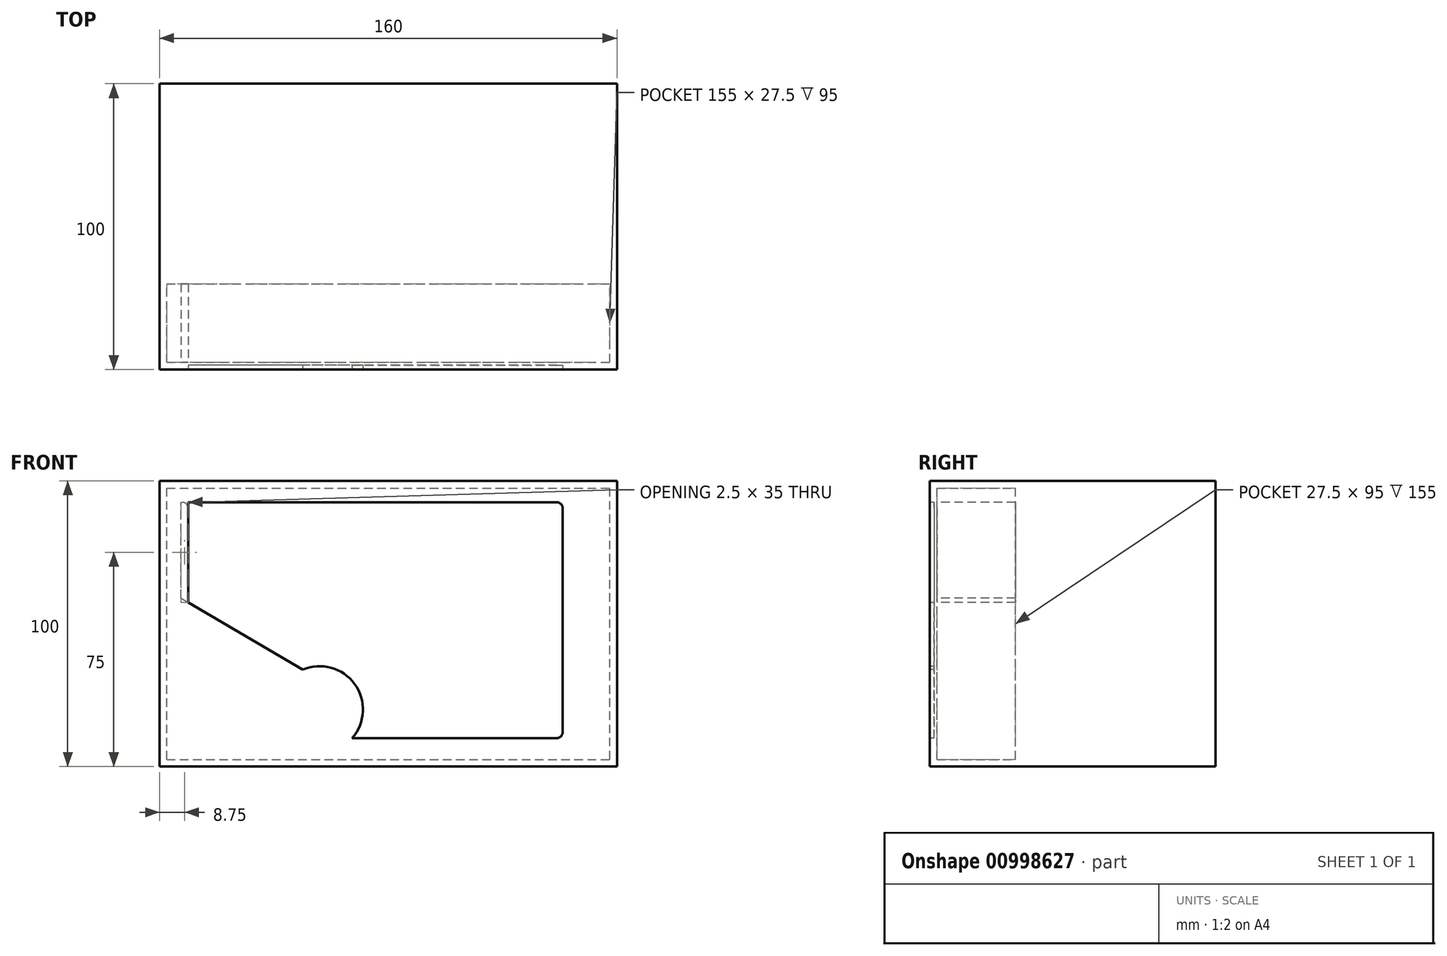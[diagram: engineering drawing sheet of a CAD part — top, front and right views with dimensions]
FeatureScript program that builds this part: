
annotation { "Feature Type Name" : "Feature", "Feature Type Description" : "" }
export const myFeature = defineFeature(function(context is Context, id is Id, definition is map)
    precondition{}
    {
        {
            var Q0;
            Q0=qCreatedBy(makeId("Front.planeOp"),FACE);
            var sketch = newSketch(context, id + "F0", { "sketchPlane" : qUnion([Q0])});
            skLineSegment(sketch, "E0.bottom", {"start": v(0, 0) * mm, "end": v(160, 0) * mm});
            skLineSegment(sketch, "E0.top", {"start": v(0, 100) * mm, "end": v(160, 100) * mm});
            skLineSegment(sketch, "E0.left", {"start": v(0, 0) * mm, "end": v(0, 100) * mm});
            skLineSegment(sketch, "E0.right", {"start": v(160, 0) * mm, "end": v(160, 100) * mm});
            skSolve(sketch);
        }
        {
            var Q0;
            Q0 = qSketchRegion(id + "F0", true);
            extrude(context, id + "F1", {"entities" : qUnion([Q0]), "depth" : 100 * mm, "offsetDistance" : 25 * mm});
        }
        {
            var Q0;
            Q0=makeQuery(id+"F1.opExtrude","CAP_FACE",FACE,{"disambiguationData":[OSD([sQuery(id+"F0.wireOp",EDGE,"E0.bottom"),sQuery(id+"F0.wireOp",EDGE,"E0.top"),sQuery(id+"F0.wireOp",EDGE,"E0.left"),sQuery(id+"F0.wireOp",EDGE,"E0.right")])],"isStart":false});
            var sketch = newSketch(context, id + "F2", { "sketchPlane" : qUnion([Q0])});
            skLineSegment(sketch, "E1.bottom", {"start": v(0, 0) * mm, "end": v(160, 0) * mm});
            skLineSegment(sketch, "E1.top", {"start": v(0, 100) * mm, "end": v(160, 100) * mm});
            skLineSegment(sketch, "E1.right", {"start": v(160, 0) * mm, "end": v(160, 100) * mm});
            skLineSegment(sketch, "E2", {"start": v(141, 50) * mm, "end": v(141, 92.5) * mm});
            skLineSegment(sketch, "E3", {"start": v(80, 10) * mm, "end": v(67.37, 10) * mm});
            skLineSegment(sketch, "E4.top", {"start": v(10, 92.5) * mm, "end": v(141, 92.5) * mm});
            skLineSegment(sketch, "E4.left", {"start": v(10, 57.5) * mm, "end": v(10, 92.5) * mm});
            skLineSegment(sketch, "E4.right", {"start": v(141, 10) * mm, "end": v(141, 92.5) * mm});
            skLineSegment(sketch, "E5", {"start": v(10, 92.5) * mm, "end": v(10, 57.5) * mm});
            skLineSegment(sketch, "E6", {"start": v(10, 57.5) * mm, "end": v(50, 33.9) * mm});
            skLineSegment(sketch, "E7", {"start": v(0, 0) * mm, "end": v(56, 0) * mm});
            skArc(sketch, "E8", {"start": v(67.37, 10) * mm, "mid": v(68.25, 28.9) * mm, "end": v(50, 33.9) * mm});
            skLineSegment(sketch, "E9.trimOffspring", {"start": v(67.37, 10) * mm, "end": v(141, 10) * mm});
            skPoint(sketch, "E10.start.orphan", {"position": v(80, 0) * mm});
            skPoint(sketch, "E11.start.orphan", {"position": v(160, 50) * mm});
            skPoint(sketch, "E12.end.orphan", {"position": v(80, 92.5) * mm});
            skPoint(sketch, "E12.start.orphan", {"position": v(80, 100) * mm});
            skSolve(sketch);
        }
        {
            var Q0;
            {var subQ1=sQuery(id+"F2.wireOp",EDGE,"E4.top");Q0=makeQuery(id+"F2.imprint","IMPRINT",FACE,{"disambiguationData":[TD([[makeQuery(id+"F2.imprint","IMPRINT",EDGE,{"derivedFrom":subQ1}),-1.0]])]});}
            extrude(context, id + "F3", {"entities" : qUnion([Q0]), "operationType" : NewBodyOperationType.REMOVE, "oppositeDirection" : true, "depth" : 50 * mm, "offsetDistance" : 25 * mm});
        }
        {
            var Q0;
            Q0=makeQuery(id+"F3.boolean.opBoolean","COPY",FACE,{"derivedFrom":makeQuery(id+"F3.opExtrude","SWEPT_FACE",FACE,{"disambiguationData":[OSD([sQuery(id+"F2.wireOp",EDGE,"E5")])]})});
            var Q1;
            Q1=makeQuery(id+"F3.boolean.opBoolean","COPY",FACE,{"derivedFrom":makeQuery(id+"F3.opExtrude","SWEPT_FACE",FACE,{"disambiguationData":[OSD([sQuery(id+"F2.wireOp",EDGE,"E6")])]})});
            var Q2;
            Q2=makeQuery(id+"F3.boolean.opBoolean","COPY",FACE,{"derivedFrom":makeQuery(id+"F3.opExtrude","SWEPT_FACE",FACE,{"disambiguationData":[OSD([sQuery(id+"F2.wireOp",EDGE,"E8")])]})});
            var Q3;
            Q3=makeQuery(id+"F3.boolean.opBoolean","COPY",FACE,{"derivedFrom":makeQuery(id+"F3.opExtrude","SWEPT_FACE",FACE,{"disambiguationData":[OSD([sQuery(id+"F2.wireOp",EDGE,"E9.trimOffspring")])]})});
            var Q4;
            Q4=makeQuery(id+"F3.boolean.opBoolean","COPY",FACE,{"derivedFrom":makeQuery(id+"F3.opExtrude","SWEPT_FACE",FACE,{"disambiguationData":[OSD([sQuery(id+"F2.wireOp",EDGE,"E4.right")])]})});
            var Q5;
            Q5=makeQuery(id+"F3.boolean.opBoolean","COPY",FACE,{"derivedFrom":makeQuery(id+"F3.opExtrude","CAP_FACE",FACE,{"disambiguationData":[OSD([sQuery(id+"F2.wireOp",EDGE,"E4.top"),sQuery(id+"F2.wireOp",EDGE,"E4.right"),sQuery(id+"F2.wireOp",EDGE,"E5"),sQuery(id+"F2.wireOp",EDGE,"E6"),sQuery(id+"F2.wireOp",EDGE,"E8"),sQuery(id+"F2.wireOp",EDGE,"E9.trimOffspring")])],"isStart":false})});
            var Q6;
            Q6=makeQuery(id+"F3.boolean.opBoolean","COPY",FACE,{"derivedFrom":makeQuery(id+"F3.opExtrude","SWEPT_FACE",FACE,{"disambiguationData":[OSD([sQuery(id+"F2.wireOp",EDGE,"E4.top")])]})});
            shell(context, id + "F4", {"entities" : qUnion([Q0, Q1, Q2, Q3, Q4, Q5, Q6]), "thickness" : 2.5 * mm});
        }
        {
            var Q0;
            {var subQ0=sQuery(id+"F0.wireOp",EDGE,"E0.right");var subQ1=sQuery(id+"F0.wireOp",EDGE,"E0.left");var subQ2=sQuery(id+"F0.wireOp",EDGE,"E0.top");var subQ3=sQuery(id+"F0.wireOp",EDGE,"E0.bottom");Q0=makeQuery(id+"F4.opShell","OFFSET_FACE",FACE,{"disambiguationData":[OSD([subQ3,subQ2,subQ1,subQ0]),TDD([makeQuery(id+"F1.opExtrude","CAP_FACE",FACE,{"disambiguationData":[OSD([subQ3,subQ2,subQ1,subQ0])],"isStart":true})])]});}
            var sketch = newSketch(context, id + "F5", { "sketchPlane" : qUnion([Q0])});
            skLineSegment(sketch, "E13.bottom", {"start": v(2.5, 97.5) * mm, "end": v(157.5, 97.5) * mm});
            skLineSegment(sketch, "E13.top", {"start": v(2.5, 2.5) * mm, "end": v(157.5, 2.5) * mm});
            skLineSegment(sketch, "E13.left", {"start": v(2.5, 97.5) * mm, "end": v(2.5, 2.5) * mm});
            skLineSegment(sketch, "E13.right", {"start": v(157.5, 97.5) * mm, "end": v(157.5, 2.5) * mm});
            skSolve(sketch);
        }
        {
            var Q0;
            Q0 = qSketchRegion(id + "F5", true);
            extrude(context, id + "F6", {"entities" : qUnion([Q0]), "operationType" : NewBodyOperationType.ADD, "depth" : 67.5 * mm, "offsetDistance" : 25 * mm});
        }
        {
            var Q0;
            Q0=makeQuery(id+"F1.opExtrude","CAP_FACE",FACE,{"disambiguationData":[OSD([sQuery(id+"F0.wireOp",EDGE,"E0.bottom"),sQuery(id+"F0.wireOp",EDGE,"E0.top"),sQuery(id+"F0.wireOp",EDGE,"E0.left"),sQuery(id+"F0.wireOp",EDGE,"E0.right")])],"isStart":false});
            cPlane(context, id + "F7", {"entities" : qUnion([Q0]), "cplaneType" : CPlaneType.OFFSET, "offset" : 2.5 * mm, "oppositeDirection" : true, "width" : 150 * mm, "height" : 150 * mm});
        }
        {
            var Q0;
            Q0=qCreatedBy(id+"F7.planeOp",FACE);
            var sketch = newSketch(context, id + "F8", { "sketchPlane" : qUnion([Q0])});
            skLineSegment(sketch, "E14", {"start": v(0, 95) * mm, "end": v(5, 95) * mm});
            skLineSegment(sketch, "E15", {"start": v(160, 0) * mm, "end": v(150.3, 0) * mm});
            skLineSegment(sketch, "E16", {"start": v(160, 5) * mm, "end": v(155, 5) * mm});
            skLineSegment(sketch, "E17.bottom", {"start": v(5, 95) * mm, "end": v(155, 95) * mm});
            skLineSegment(sketch, "E17.top", {"start": v(5, 5) * mm, "end": v(155, 5) * mm});
            skLineSegment(sketch, "E17.left", {"start": v(5, 95) * mm, "end": v(5, 5) * mm});
            skLineSegment(sketch, "E17.right", {"start": v(155, 95) * mm, "end": v(155, 5) * mm});
            skSolve(sketch);
        }
        {
            var Q0;
            Q0 = qSketchRegion(id + "F8", true);
            extrude(context, id + "F9", {"entities" : qUnion([Q0]), "operationType" : NewBodyOperationType.ADD, "depth" : 1 * mm, "offsetDistance" : 25 * mm});
        }
        {
            var Q0;
            Q0=makeQuery(id+"F3.boolean.opBoolean","COPY",EDGE,{"derivedFrom":makeQuery(id+"F3.opExtrude","SWEPT_EDGE",EDGE,{"disambiguationData":[OSD([sQuery(id+"F2.wireOp",EDGE,"E4.top"),sQuery(id+"F2.wireOp",EDGE,"E5")])]})});
            var Q1;
            Q1=makeQuery(id+"F3.boolean.opBoolean","COPY",EDGE,{"derivedFrom":makeQuery(id+"F3.opExtrude","SWEPT_EDGE",EDGE,{"disambiguationData":[OSD([sQuery(id+"F2.wireOp",EDGE,"E4.top"),sQuery(id+"F2.wireOp",EDGE,"E4.right")])]})});
            var Q2;
            Q2=makeQuery(id+"F3.boolean.opBoolean","COPY",EDGE,{"derivedFrom":makeQuery(id+"F3.opExtrude","SWEPT_EDGE",EDGE,{"disambiguationData":[OSD([sQuery(id+"F2.wireOp",EDGE,"E4.right"),sQuery(id+"F2.wireOp",EDGE,"E9.trimOffspring")])]})});
            fillet(context, id + "F10", {"entities" : qUnion([Q0, Q1, Q2]), "radius" : 2 * mm, "tangentPropagation" : true, "allowEdgeOverflow" : false});
        }
    });
